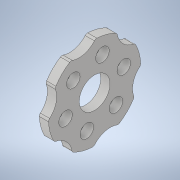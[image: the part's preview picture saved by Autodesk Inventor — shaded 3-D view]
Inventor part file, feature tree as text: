
AUTODESK INVENTOR PART (.ipt)
format: ipt  version: 2021 (Build 250183000, 183)  size: 174,592 bytes
history: native  units: in
note: dims shown in document units (in); Inventor stores cm internally (conversion verified against a paired STEP export)
features: extrude x1, fillet x1, sketch x1
ambient origin geometry x8: Origin, YZ Plane, XZ Plane, XY Plane, X Axis, Y Axis, Z Axis, Center Point
bodies: Solid1 (feature_tree)
feature tree (3):
  extrude  "Extrusion1"  Depth=2.451in
  fillet  "Fillet1"  Radius=0.55in
  sketch  "Sketch1"  dims[d0=3.75in d1=2.451in d2=0.55in d3=45.0deg d4=2.3622in d6=360.0deg d8=1.25in d12=1.65in d16=15.0deg d17=2.3622in d19=360.0deg d21=0.375in d22=0.0in d23=0.125in]
